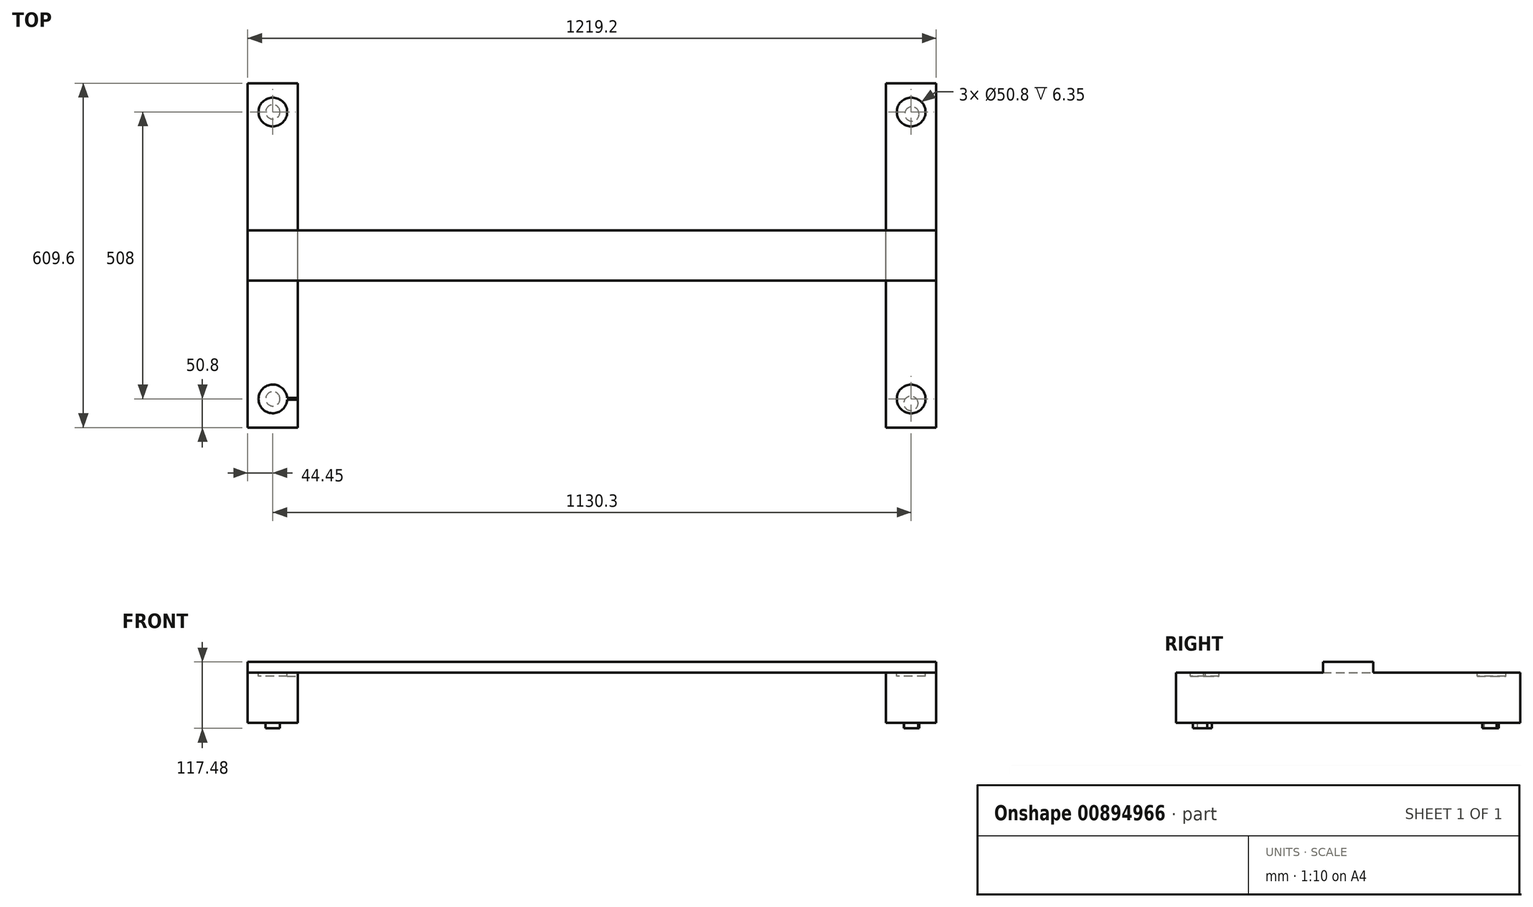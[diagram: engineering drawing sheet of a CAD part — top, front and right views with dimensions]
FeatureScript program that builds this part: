
annotation { "Feature Type Name" : "Feature", "Feature Type Description" : "" }
export const myFeature = defineFeature(function(context is Context, id is Id, definition is map)
    precondition{}
    {
        {
            var Q0;
            Q0=qCreatedBy(makeId("Top.planeOp"),FACE);
            var sketch = newSketch(context, id + "F0", { "sketchPlane" : qUnion([Q0])});
            skLineSegment(sketch, "E0.bottom", {"start": v(-609.6, 44.45) * mm, "end": v(609.6, 44.45) * mm});
            skLineSegment(sketch, "E0.top", {"start": v(-609.6, -44.45) * mm, "end": v(609.6, -44.45) * mm});
            skLineSegment(sketch, "E0.left", {"start": v(-609.6, 44.45) * mm, "end": v(-609.6, -44.45) * mm});
            skLineSegment(sketch, "E0.right", {"start": v(609.6, 44.45) * mm, "end": v(609.6, -44.45) * mm});
            skLineSegment(sketch, "E1", {"start": v(-609.6, 44.45) * mm, "end": v(609.6, -44.45) * mm, "construction": true});
            skLineSegment(sketch, "E2", {"start": v(609.6, 44.45) * mm, "end": v(-609.6, -44.45) * mm, "construction": true});
            skSolve(sketch);
        }
        {
            var Q0;
            Q0 = qSketchRegion(id + "F0", true);
            var Q1;
            Q1=makeQuery(id+"F0.imprint","IMPRINT",FACE,{"disambiguationData":[TD([[makeQuery(id+"F0.imprint","IMPRINT",EDGE,{"derivedFrom":sQuery(id+"F0.wireOp",EDGE,"E0.bottom")}),-1.0]])]});
            extrude(context, id + "F1", {"entities" : qUnion([Q0, Q1]), "depth" : 19.05 * mm, "offsetDistance" : 25.4 * mm});
        }
        {
            var Q0;
            Q0=makeQuery(id+"F1.opExtrude","CAP_FACE",FACE,{"disambiguationData":[OSD([sQuery(id+"F0.wireOp",EDGE,"E0.bottom"),sQuery(id+"F0.wireOp",EDGE,"E0.top"),sQuery(id+"F0.wireOp",EDGE,"E0.left"),sQuery(id+"F0.wireOp",EDGE,"E0.right")])],"isStart":true});
            var sketch = newSketch(context, id + "F2", { "sketchPlane" : qUnion([Q0])});
            skLineSegment(sketch, "E3.bottom", {"start": v(-609.6, 304.8) * mm, "end": v(-520.7, 304.8) * mm});
            skLineSegment(sketch, "E3.top", {"start": v(-609.6, -304.8) * mm, "end": v(-520.7, -304.8) * mm});
            skLineSegment(sketch, "E3.left", {"start": v(-609.6, 304.8) * mm, "end": v(-609.6, -304.8) * mm});
            skLineSegment(sketch, "E3.right", {"start": v(-520.7, 304.8) * mm, "end": v(-520.7, -304.8) * mm});
            skSolve(sketch);
        }
        {
            var Q0;
            Q0 = qSketchRegion(id + "F2", true);
            extrude(context, id + "F3", {"entities" : qUnion([Q0]), "operationType" : NewBodyOperationType.ADD, "depth" : 88.9 * mm, "offsetDistance" : 25.4 * mm});
        }
        {
            var Q0;
            Q0=makeQuery(id+"F1.opExtrude","CAP_FACE",FACE,{"disambiguationData":[OSD([sQuery(id+"F0.wireOp",EDGE,"E0.bottom"),sQuery(id+"F0.wireOp",EDGE,"E0.top"),sQuery(id+"F0.wireOp",EDGE,"E0.left"),sQuery(id+"F0.wireOp",EDGE,"E0.right")])],"isStart":true});
            var sketch = newSketch(context, id + "F4", { "sketchPlane" : qUnion([Q0])});
            skLineSegment(sketch, "E4.bottom", {"start": v(520.7, 304.8) * mm, "end": v(609.6, 304.8) * mm});
            skLineSegment(sketch, "E4.top", {"start": v(520.7, -304.8) * mm, "end": v(609.6, -304.8) * mm});
            skLineSegment(sketch, "E4.left", {"start": v(520.7, 304.8) * mm, "end": v(520.7, -304.8) * mm});
            skLineSegment(sketch, "E4.right", {"start": v(609.6, 304.8) * mm, "end": v(609.6, -304.8) * mm});
            skSolve(sketch);
        }
        {
            var Q0;
            Q0 = qSketchRegion(id + "F4", true);
            extrude(context, id + "F5", {"entities" : qUnion([Q0]), "operationType" : NewBodyOperationType.ADD, "depth" : 88.9 * mm, "offsetDistance" : 25.4 * mm});
        }
        {
            var Q0;
            Q0=makeQuery(id+"F3.opExtrude","CAP_FACE",FACE,{"disambiguationData":[OSD([sQuery(id+"F2.wireOp",EDGE,"E3.bottom"),sQuery(id+"F2.wireOp",EDGE,"E3.top"),sQuery(id+"F2.wireOp",EDGE,"E3.left"),sQuery(id+"F2.wireOp",EDGE,"E3.right")])],"isStart":false});
            var sketch = newSketch(context, id + "F6", { "sketchPlane" : qUnion([Q0])});
            skLineSegment(sketch, "E5", {"start": v(-565.15, -304.8) * mm, "end": v(-565.15, -254) * mm, "construction": true});
            skLineSegment(sketch, "E6", {"start": v(-565.15, 304.8) * mm, "end": v(-565.15, 254) * mm, "construction": true});
            skLineSegment(sketch, "E7", {"start": v(564.73, 312.67) * mm, "end": v(564.73, 261.87) * mm, "construction": true});
            skLineSegment(sketch, "E8", {"start": v(566.57, -301.16) * mm, "end": v(566.57, -250.36) * mm, "construction": true});
            skCircle(sketch, "E9", {"center": v(-565.15, 254) * mm, "radius": 12.7 * mm});
            skCircle(sketch, "E10", {"center": v(-565.15, -254) * mm, "radius": 12.7 * mm});
            skCircle(sketch, "E11", {"center": v(564.73, 261.87) * mm, "radius": 12.7 * mm});
            skCircle(sketch, "E12", {"center": v(566.57, -250.36) * mm, "radius": 12.7 * mm});
            skSolve(sketch);
        }
        {
            var Q0;
            Q0 = qSketchRegion(id + "F6", true);
            extrude(context, id + "F7", {"entities" : qUnion([Q0]), "operationType" : NewBodyOperationType.ADD, "depth" : 9.52 * mm, "offsetDistance" : 25.4 * mm});
        }
        {
            var Q0;
            {var subQ0=sQuery(id+"F2.wireOp",EDGE,"E3.bottom");var subQ2=sQuery(id+"F0.wireOp",EDGE,"E0.top");var subQ3=sQuery(id+"F2.wireOp",EDGE,"E3.left");var subQ4=sQuery(id+"F2.wireOp",EDGE,"E3.right");Q0=makeQuery(id+"F3.boolean.opBoolean","SPLIT",FACE,{"disambiguationData":[TD([makeQuery(id+"F1.opExtrude","SWEPT_FACE",FACE,{"disambiguationData":[OSD([subQ2])]})])],"derivedFrom":makeQuery(id+"F3.opExtrude","CAP_FACE",FACE,{"disambiguationData":[OSD([subQ0,sQuery(id+"F2.wireOp",EDGE,"E3.top"),subQ3,subQ4])],"isStart":true})});}
            var sketch = newSketch(context, id + "F8", { "sketchPlane" : qUnion([Q0])});
            skLineSegment(sketch, "E13", {"start": v(-565.15, -304.8) * mm, "end": v(-565.15, -254) * mm, "construction": true});
            skLineSegment(sketch, "E14", {"start": v(-565.15, 304.8) * mm, "end": v(-565.15, 254) * mm, "construction": true});
            skLineSegment(sketch, "E15", {"start": v(565.15, -304.8) * mm, "end": v(565.15, -254) * mm, "construction": true});
            skLineSegment(sketch, "E16", {"start": v(565.15, 304.8) * mm, "end": v(565.15, 254) * mm, "construction": true});
            skCircle(sketch, "E17", {"center": v(-565.15, -254) * mm, "radius": 25.4 * mm});
            skCircle(sketch, "E18", {"center": v(565.15, 254) * mm, "radius": 25.4 * mm});
            skCircle(sketch, "E19", {"center": v(565.15, -254) * mm, "radius": 25.4 * mm});
            skCircle(sketch, "E20", {"center": v(-565.15, 254) * mm, "radius": 25.4 * mm});
            skLineSegment(sketch, "E21", {"start": v(-520.7, -254) * mm, "end": v(-520.7, -252.41) * mm});
            skLineSegment(sketch, "E22", {"start": v(-520.7, -255.59) * mm, "end": v(-520.7, -254) * mm});
            skLineSegment(sketch, "E23", {"start": v(-539.8, -252.41) * mm, "end": v(-520.7, -252.41) * mm});
            skLineSegment(sketch, "E24", {"start": v(-539.8, -255.59) * mm, "end": v(-520.7, -255.59) * mm});
            skSolve(sketch);
        }
        {
            var Q0;
            Q0=makeQuery(id+"F8.imprint","IMPRINT",FACE,{"disambiguationData":[TD([[makeQuery(id+"F8.imprint","IMPRINT",EDGE,{"derivedFrom":sQuery(id+"F8.wireOp",EDGE,"E17")}),1.0]])]});
            var Q1;
            Q1=makeQuery(id+"F8.imprint","IMPRINT",FACE,{"disambiguationData":[TD([[makeQuery(id+"F8.imprint","IMPRINT",EDGE,{"derivedFrom":sQuery(id+"F8.wireOp",EDGE,"E20")}),1.0]])]});
            var Q2;
            Q2=makeQuery(id+"F8.imprint","IMPRINT",FACE,{"disambiguationData":[TD([[makeQuery(id+"F8.imprint","IMPRINT",EDGE,{"derivedFrom":sQuery(id+"F8.wireOp",EDGE,"E18")}),1.0]])]});
            var Q3;
            Q3=makeQuery(id+"F8.imprint","IMPRINT",FACE,{"disambiguationData":[TD([[makeQuery(id+"F8.imprint","IMPRINT",EDGE,{"derivedFrom":sQuery(id+"F8.wireOp",EDGE,"E19")}),1.0]])]});
            var Q4;
            Q4=makeQuery(id+"F8.imprint","IMPRINT",FACE,{"disambiguationData":[TD([[makeQuery(id+"F8.imprint","IMPRINT",EDGE,{"derivedFrom":sQuery(id+"F8.wireOp",EDGE,"E21")}),1.0]])]});
            extrude(context, id + "F9", {"entities" : qUnion([Q0, Q1, Q2, Q3, Q4]), "operationType" : NewBodyOperationType.REMOVE, "oppositeDirection" : true, "depth" : 6.35 * mm, "offsetDistance" : 25.4 * mm});
        }
    });
